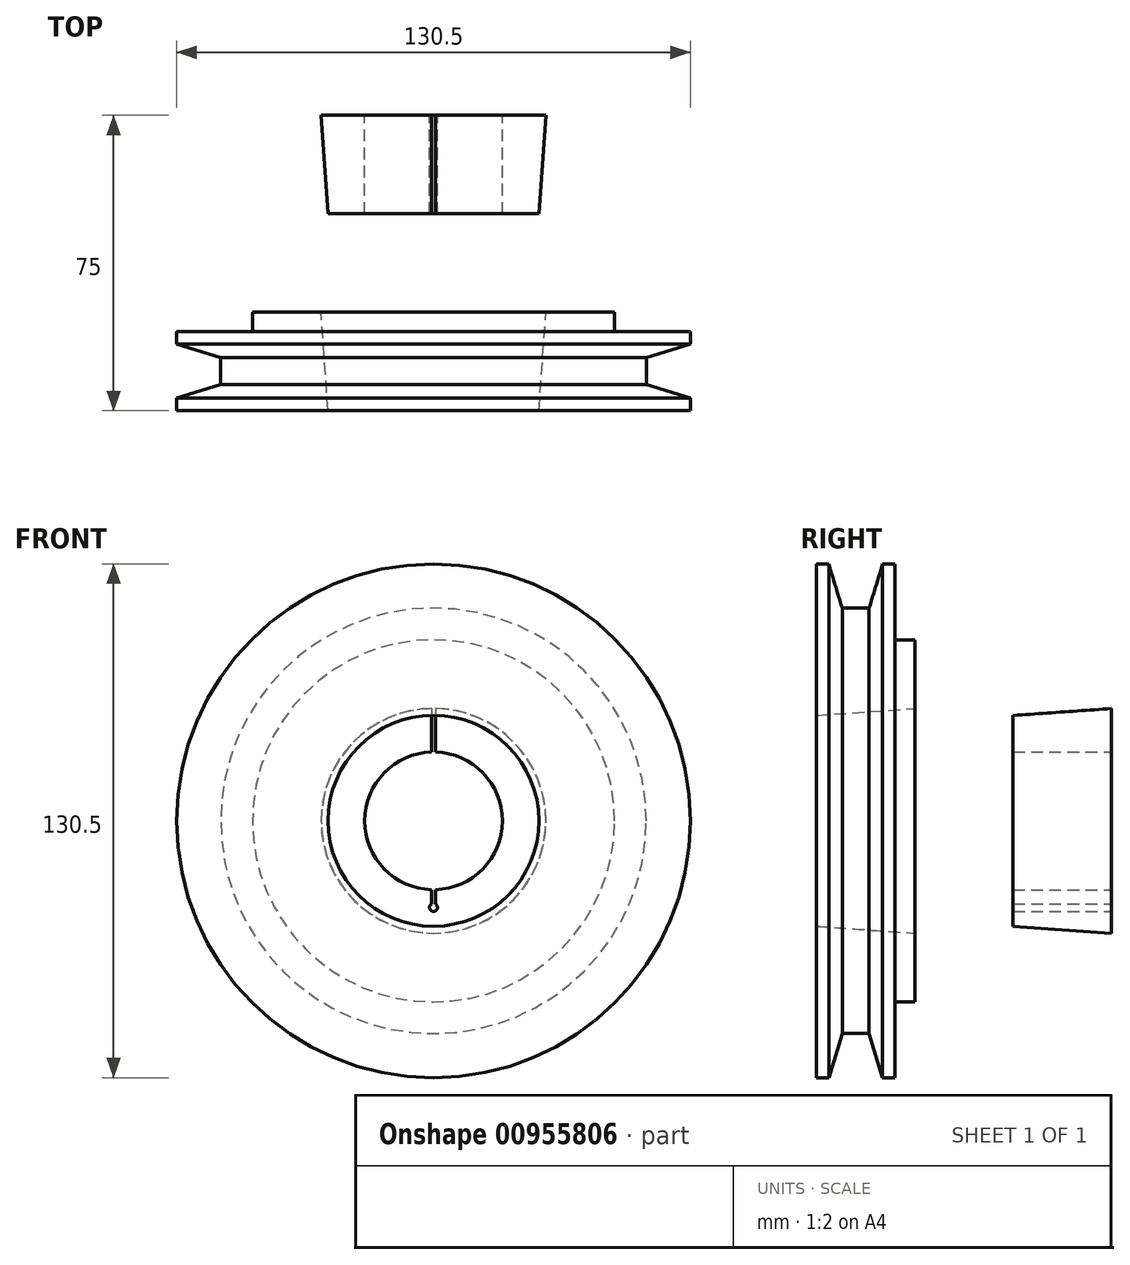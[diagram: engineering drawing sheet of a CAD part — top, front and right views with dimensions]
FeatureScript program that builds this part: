
annotation { "Feature Type Name" : "Feature", "Feature Type Description" : "" }
export const myFeature = defineFeature(function(context is Context, id is Id, definition is map)
    precondition{}
    {
        {
            var Q0;
            Q0=qCreatedBy(makeId("Right.planeOp"),FACE);
            var sketch = newSketch(context, id + "F0", { "sketchPlane" : qUnion([Q0])});
            skLineSegment(sketch, "E0", {"start": v(0, 0) * mm, "end": v(0, 65.25) * mm});
            skLineSegment(sketch, "E1", {"start": v(20, 65.25) * mm, "end": v(20, 46) * mm});
            skLineSegment(sketch, "E2", {"start": v(20, 46) * mm, "end": v(25, 46) * mm});
            skLineSegment(sketch, "E3", {"start": v(25, 46) * mm, "end": v(25, 0) * mm});
            skLineSegment(sketch, "E4", {"start": v(25, 0) * mm, "end": v(0, 0) * mm});
            skLineSegment(sketch, "E5", {"start": v(0, 65.25) * mm, "end": v(3.15, 65.25) * mm});
            skLineSegment(sketch, "E6", {"start": v(3.15, 65.25) * mm, "end": v(6.57, 54.05) * mm});
            skLineSegment(sketch, "E7", {"start": v(6.57, 54.05) * mm, "end": v(13.43, 54.05) * mm});
            skLineSegment(sketch, "E8", {"start": v(13.43, 54.05) * mm, "end": v(16.85, 65.25) * mm});
            skLineSegment(sketch, "E9", {"start": v(16.85, 65.25) * mm, "end": v(20, 65.25) * mm});
            skSolve(sketch);
        }
        {
            var Q0;
            Q0=makeQuery(id+"F0.imprint","IMPRINT",FACE,{"disambiguationData":[TD([[makeQuery(id+"F0.imprint","IMPRINT",EDGE,{"derivedFrom":sQuery(id+"F0.wireOp",EDGE,"E0")}),-1.0]])]});
            var Q1;
            Q1=sQuery(id+"F0.wireOp",EDGE,"E4");
            revolve(context, id + "F1", {"entities" : qUnion([Q0]), "axis" : qUnion([Q1]), "revolveType" : RevolveType.FULL});
        }
        {
            var Q0;
            Q0=makeQuery(id+"F1.opRevolve","SWEPT_FACE",FACE,{"disambiguationData":[OSD([sQuery(id+"F0.wireOp",EDGE,"E0")])]});
            var sketch = newSketch(context, id + "F2", { "sketchPlane" : qUnion([Q0])});
            skCircle(sketch, "E10", {"center": v(0, 0) * mm, "radius": 26.8 * mm});
            skSolve(sketch);
        }
        {
            var Q0;
            Q0=qSketchRegion(id+"F2",true);
            extrude(context, id + "F3", {"entities" : qUnion([Q0]), "operationType" : NewBodyOperationType.REMOVE, "oppositeDirection" : true, "depth" : 25 * mm, "hasDraft" : true, "draftAngle" : 4 * degree});
        }
        {
            var Q0;
            Q0=makeQuery(id+"F1.opRevolve","SWEPT_FACE",FACE,{"disambiguationData":[OSD([sQuery(id+"F0.wireOp",EDGE,"E3")])]});
            cPlane(context, id + "F4", {"entities" : qUnion([Q0]), "cplaneType" : CPlaneType.OFFSET, "offset" : 25 * mm, "width" : 150 * mm, "height" : 150 * mm});
        }
        {
            var Q0;
            Q0=qCreatedBy(id+"F4.planeOp",FACE);
            var sketch = newSketch(context, id + "F5", { "sketchPlane" : qUnion([Q0])});
            skCircle(sketch, "E11", {"center": v(0, 0) * mm, "radius": 26.79 * mm});
            skSolve(sketch);
        }
        {
            var Q0;
            Q0=qSketchRegion(id+"F5",true);
            extrude(context, id + "F6", {"entities" : qUnion([Q0]), "depth" : 25 * mm, "hasDraft" : true, "draftAngle" : 4 * degree});
        }
        {
            var Q0;
            Q0=makeQuery(id+"F6.opExtrude","CAP_FACE",FACE,{"disambiguationData":[OSD([sQuery(id+"F5.wireOp",EDGE,"E11")])],"isStart":false});
            var sketch = newSketch(context, id + "F7", { "sketchPlane" : qUnion([Q0])});
            skCircle(sketch, "E12", {"center": v(0, 0) * mm, "radius": 17.5 * mm});
            skSolve(sketch);
        }
        {
            var Q0;
            Q0=qSketchRegion(id+"F7",true);
            var Q1;
            Q1=makeQuery(id+"F6.opExtrude","CAP_FACE",FACE,{"disambiguationData":[OSD([sQuery(id+"F5.wireOp",EDGE,"E11")])],"isStart":true});
            extrude(context, id + "F8", {"entities" : qUnion([Q0]), "operationType" : NewBodyOperationType.REMOVE, "endBound" : BoundingType.UP_TO_SURFACE, "oppositeDirection" : true, "endBoundEntityFace" : qUnion([Q1]), "depth" : 25 * mm});
        }
        {
            var Q0;
            Q0=makeQuery(id+"F6.opExtrude","CAP_FACE",FACE,{"disambiguationData":[OSD([sQuery(id+"F5.wireOp",EDGE,"E11")])],"isStart":false});
            var sketch = newSketch(context, id + "F9", { "sketchPlane" : qUnion([Q0])});
            skLineSegment(sketch, "E13.bottom", {"start": v(0.5, 30) * mm, "end": v(-0.5, 30) * mm});
            skLineSegment(sketch, "E13.top", {"start": v(0.5, -22) * mm, "end": v(-0.5, -22) * mm});
            skLineSegment(sketch, "E13.left", {"start": v(0.5, 30) * mm, "end": v(0.5, -22) * mm});
            skLineSegment(sketch, "E13.right", {"start": v(-0.5, 30) * mm, "end": v(-0.5, -22) * mm});
            skPoint(sketch, "E13.middle", {"position": v(0, 4) * mm});
            skCircle(sketch, "E14", {"center": v(0, -22) * mm, "radius": 1 * mm});
            skSolve(sketch);
        }
        {
            var Q0;
            Q0=qSketchRegion(id+"F9",true);
            var Q1;
            Q1=makeQuery(id+"F6.opExtrude","CAP_FACE",FACE,{"disambiguationData":[OSD([sQuery(id+"F5.wireOp",EDGE,"E11")])],"isStart":true});
            extrude(context, id + "F10", {"entities" : qUnion([Q0]), "operationType" : NewBodyOperationType.REMOVE, "endBound" : BoundingType.UP_TO_SURFACE, "oppositeDirection" : true, "endBoundEntityFace" : qUnion([Q1]), "depth" : 25 * mm});
        }
    });
